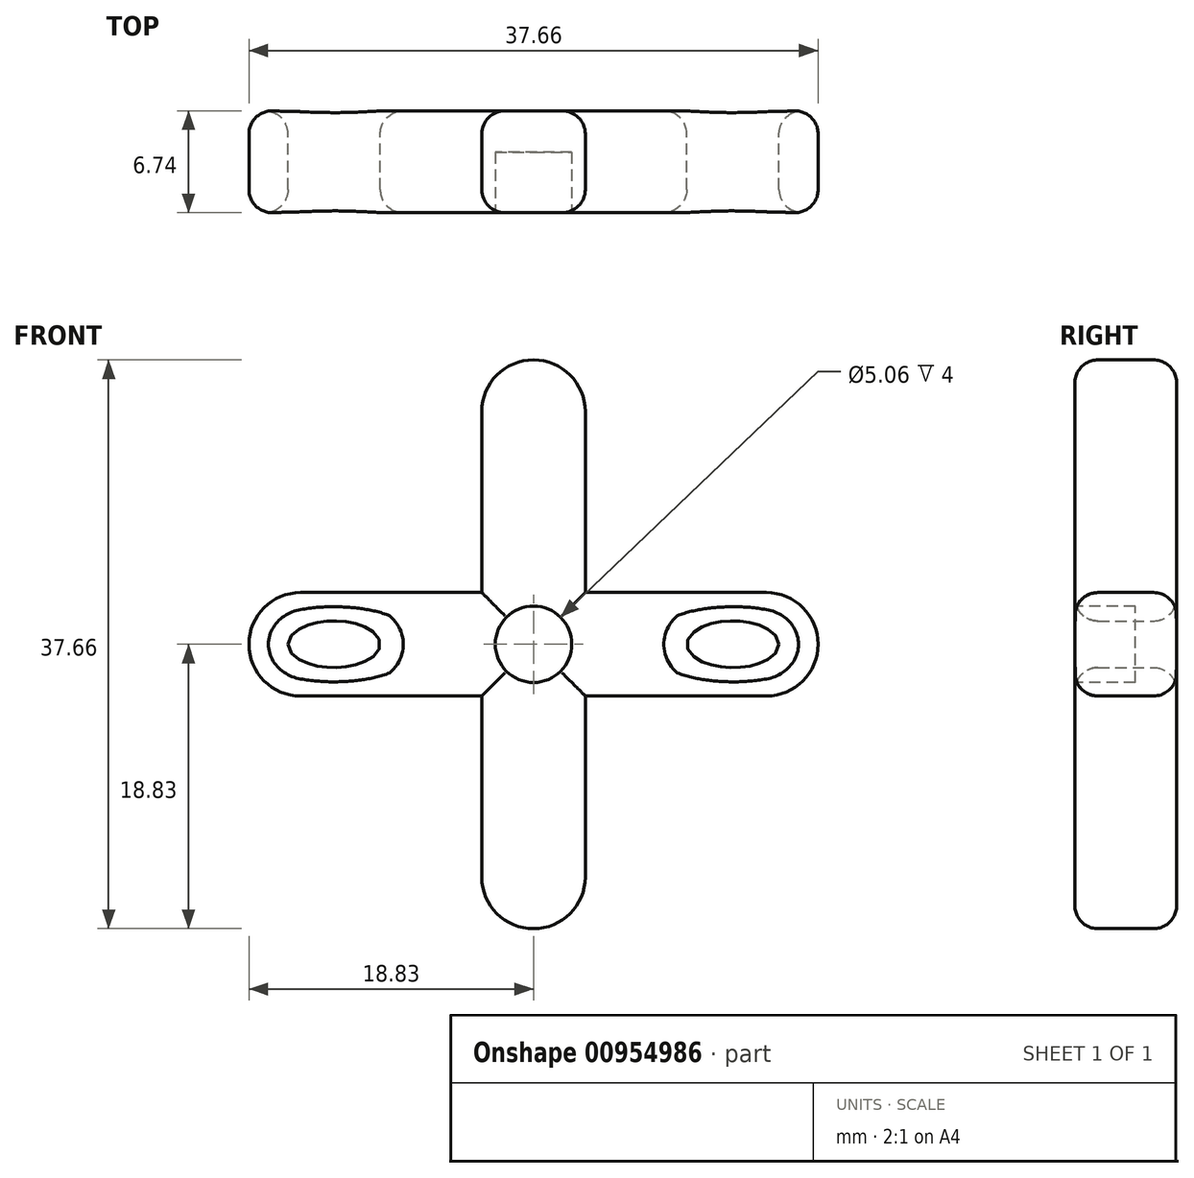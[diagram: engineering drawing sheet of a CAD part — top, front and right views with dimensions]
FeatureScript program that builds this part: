
annotation { "Feature Type Name" : "Feature", "Feature Type Description" : "" }
export const myFeature = defineFeature(function(context is Context, id is Id, definition is map)
    precondition{}
    {
        {
            var Q0;
            Q0=qCreatedBy(makeId("Front.planeOp"),FACE);
            var sketch = newSketch(context, id + "F0", { "sketchPlane" : qUnion([Q0])});
            skLineSegment(sketch, "E0.bottom", {"start": v(11.43, 2.54) * mm, "end": v(-11.43, 2.54) * mm});
            skLineSegment(sketch, "E0.top", {"start": v(11.43, -2.54) * mm, "end": v(-11.43, -2.54) * mm});
            skLineSegment(sketch, "E0.left", {"start": v(11.43, 2.54) * mm, "end": v(11.43, -2.54) * mm});
            skLineSegment(sketch, "E0.right", {"start": v(-11.43, 2.54) * mm, "end": v(-11.43, -2.54) * mm});
            skPoint(sketch, "E0.middle", {"position": v(0, 0) * mm});
            skLineSegment(sketch, "E1.bottom", {"start": v(2.54, 11.43) * mm, "end": v(-2.54, 11.43) * mm});
            skLineSegment(sketch, "E1.top", {"start": v(2.54, -11.43) * mm, "end": v(-2.54, -11.43) * mm});
            skLineSegment(sketch, "E1.left", {"start": v(2.54, 11.43) * mm, "end": v(2.54, -11.43) * mm});
            skLineSegment(sketch, "E1.right", {"start": v(-2.54, 11.43) * mm, "end": v(-2.54, -11.43) * mm});
            skArc(sketch, "E2", {"start": v(11.43, 2.54) * mm, "mid": v(13.97, 0) * mm, "end": v(11.43, -2.54) * mm});
            skArc(sketch, "E3", {"start": v(-11.43, 2.54) * mm, "mid": v(-13.97, 0) * mm, "end": v(-11.43, -2.54) * mm});
            skArc(sketch, "E4", {"start": v(2.54, 11.43) * mm, "mid": v(0, 13.97) * mm, "end": v(-2.54, 11.43) * mm});
            skArc(sketch, "E5", {"start": v(-2.54, -11.43) * mm, "mid": v(0, -13.97) * mm, "end": v(2.54, -11.43) * mm});
            skEllipse(sketch, "E6", {"center": v(9.79, 0) * mm, "majorRadius": 2.26 * mm, "minorRadius": 1.15 * mm, "majorAxis": v(1, 0)});
            skEllipse(sketch, "E7.MirrorC", {"center": v(9.79, 0) * mm, "majorRadius": 2.26 * mm, "minorRadius": 1.15 * mm, "majorAxis": v(-1, 0)});
            skEllipse(sketch, "E8.MirrorC", {"center": v(-9.79, 0) * mm, "majorRadius": 2.26 * mm, "minorRadius": 1.15 * mm, "majorAxis": v(-1, 0)});
            skEllipse(sketch, "E9", {"center": v(0, 8.8) * mm, "majorRadius": 1.78 * mm, "minorRadius": 1.1 * mm, "majorAxis": v(0, 1)});
            skEllipse(sketch, "E10.MirrorC", {"center": v(0, -8.8) * mm, "majorRadius": 1.78 * mm, "minorRadius": 1.1 * mm, "majorAxis": v(0, -1)});
            skFitSpline(sketch, "E11.0", {"points": [v(0.5, 10.6) * mm, v(0, 10.76) * mm, v(-0.5, 10.6) * mm, v(-0.9, 10.15) * mm, v(-1.16, 9.53) * mm, v(-1.25, 8.8) * mm, v(-1.16, 8.07) * mm, v(-0.9, 7.44) * mm, v(-0.5, 7) * mm, v(0, 6.83) * mm, v(0.5, 7) * mm, v(0.9, 7.44) * mm, v(1.16, 8.07) * mm, v(1.25, 8.8) * mm, v(1.16, 9.53) * mm, v(0.9, 10.15) * mm, v(0.5, 10.6) * mm, v(0, 10.76) * mm, v(-0.5, 10.6) * mm, v(0.5, 10.6) * mm]});
            skEllipse(sketch, "E12.MirrorC", {"center": v(9.79, 0) * mm, "majorRadius": 2.26 * mm, "minorRadius": 1.15 * mm, "majorAxis": v(-1, 0)});
            skFitSpline(sketch, "E13.0", {"points": [v(12.14, -0.27) * mm, v(12.2, 0) * mm, v(12.14, 0.27) * mm, v(11.94, 0.6) * mm, v(11.49, 0.95) * mm, v(10.7, 1.21) * mm, v(9.79, 1.3) * mm, v(8.88, 1.21) * mm, v(8.1, 0.95) * mm, v(7.64, 0.6) * mm, v(7.44, 0.27) * mm, v(7.38, 0) * mm, v(7.44, -0.27) * mm, v(7.64, -0.6) * mm, v(8.1, -0.95) * mm, v(8.88, -1.21) * mm, v(9.79, -1.3) * mm, v(10.7, -1.21) * mm, v(11.49, -0.95) * mm, v(11.94, -0.6) * mm, v(12.14, -0.27) * mm, v(12.2, 0) * mm, v(12.14, 0.27) * mm, v(12.14, -0.27) * mm]});
            skFitSpline(sketch, "E14.0", {"points": [v(-12.15, 0.27) * mm, v(-12.2, 0) * mm, v(-12.15, -0.27) * mm, v(-11.94, -0.6) * mm, v(-11.49, -0.95) * mm, v(-10.7, -1.21) * mm, v(-9.79, -1.3) * mm, v(-8.87, -1.21) * mm, v(-8.1, -0.95) * mm, v(-7.64, -0.6) * mm, v(-7.43, -0.27) * mm, v(-7.38, 0) * mm, v(-7.43, 0.27) * mm, v(-7.64, 0.6) * mm, v(-8.1, 0.95) * mm, v(-8.87, 1.21) * mm, v(-9.79, 1.3) * mm, v(-10.7, 1.21) * mm, v(-11.49, 0.95) * mm, v(-11.94, 0.6) * mm, v(-12.15, 0.27) * mm, v(-12.2, 0) * mm, v(-12.15, -0.27) * mm, v(-12.15, 0.27) * mm]});
            skFitSpline(sketch, "E15.0", {"points": [v(-0.52, -10.61) * mm, v(0, -10.78) * mm, v(0.52, -10.61) * mm, v(0.93, -10.16) * mm, v(1.18, -9.53) * mm, v(1.27, -8.8) * mm, v(1.18, -8.06) * mm, v(0.93, -7.43) * mm, v(0.52, -6.98) * mm, v(0, -6.8) * mm, v(-0.52, -6.98) * mm, v(-0.93, -7.43) * mm, v(-1.18, -8.06) * mm, v(-1.27, -8.8) * mm, v(-1.18, -9.53) * mm, v(-0.93, -10.16) * mm, v(-0.52, -10.61) * mm, v(0, -10.78) * mm, v(0.52, -10.61) * mm, v(-0.52, -10.61) * mm]});
            skSolve(sketch);
        }
        {
            var Q0;
            Q0=makeQuery(id+"F0.imprint","IMPRINT",FACE,{"disambiguationData":[TD([[makeQuery(id+"F0.imprint","IMPRINT",EDGE,{"derivedFrom":sQuery(id+"F0.wireOp",EDGE,"E1.bottom")}),-1.0]])]});
            var Q1;
            {var subQ0=sQuery(id+"F0.wireOp",EDGE,"E12.MirrorC");var subQ1=sQuery(id+"F0.wireOp",EDGE,"E0.left");var subQ2=makeQuery(id+"F0.imprint","INTERSECT",VERTEX,{"disambiguationData":[OD(0.0)],"derivedFrom":[subQ1,subQ0]});Q1=makeQuery(id+"F0.imprint","IMPRINT",FACE,{"disambiguationData":[TD([[makeQuery(id+"F0.imprint","IMPRINT",EDGE,{"disambiguationData":[TD([[subQ2,-1.0]])],"derivedFrom":subQ1}),-1.0]])]});}
            var Q2;
            {var subQ2=sQuery(id+"F0.wireOp",EDGE,"E1.top");Q2=makeQuery(id+"F0.imprint","IMPRINT",FACE,{"disambiguationData":[TD([[makeQuery(id+"F0.imprint","IMPRINT",EDGE,{"derivedFrom":subQ2}),-1.0]])]});}
            var Q3;
            {var subQ0=sQuery(id+"F0.wireOp",EDGE,"E3");Q3=makeQuery(id+"F0.imprint","IMPRINT",FACE,{"disambiguationData":[TD([[makeQuery(id+"F0.imprint","IMPRINT",EDGE,{"derivedFrom":subQ0}),1.0]])]});}
            var Q4;
            Q4=makeQuery(id+"F0.imprint","IMPRINT",FACE,{"disambiguationData":[TD([[makeQuery(id+"F0.imprint","IMPRINT",EDGE,{"derivedFrom":sQuery(id+"F0.wireOp",EDGE,"E9")}),1.0]])]});
            var Q5;
            {var subQ0=sQuery(id+"F0.wireOp",EDGE,"E1.left");var subQ1=sQuery(id+"F0.wireOp",EDGE,"E0.bottom");var subQ2=makeQuery(id+"F0.imprint","INTERSECT",VERTEX,{"derivedFrom":[subQ1,subQ0]});Q5=makeQuery(id+"F0.imprint","IMPRINT",FACE,{"disambiguationData":[TD([[makeQuery(id+"F0.imprint","IMPRINT",EDGE,{"disambiguationData":[TD([[subQ2,-1.0]])],"derivedFrom":subQ1}),1.0]])]});}
            var Q6;
            Q6=makeQuery(id+"F0.imprint","IMPRINT",FACE,{"disambiguationData":[TD([[makeQuery(id+"F0.imprint","IMPRINT",EDGE,{"derivedFrom":sQuery(id+"F0.wireOp",EDGE,"E1.top")}),1.0]])]});
            var Q7;
            {var subQ0=sQuery(id+"F0.wireOp",EDGE,"E2");Q7=makeQuery(id+"F0.imprint","IMPRINT",FACE,{"disambiguationData":[TD([[makeQuery(id+"F0.imprint","IMPRINT",EDGE,{"derivedFrom":subQ0}),-1.0]])]});}
            var Q8;
            {var subQ0=sQuery(id+"F0.wireOp",EDGE,"E8.MirrorC");var subQ1=sQuery(id+"F0.wireOp",EDGE,"E0.right");var subQ2=makeQuery(id+"F0.imprint","INTERSECT",VERTEX,{"disambiguationData":[OD(0.0)],"derivedFrom":[subQ1,subQ0]});Q8=makeQuery(id+"F0.imprint","IMPRINT",FACE,{"disambiguationData":[TD([[makeQuery(id+"F0.imprint","IMPRINT",EDGE,{"disambiguationData":[TD([[subQ2,-1.0]])],"derivedFrom":subQ1}),1.0]])]});}
            var Q9;
            {var subQ2=sQuery(id+"F0.wireOp",EDGE,"E0.bottom");var subQ6=sQuery(id+"F0.wireOp",EDGE,"E1.right");var subQ7=makeQuery(id+"F0.imprint","INTERSECT",VERTEX,{"derivedFrom":[subQ2,subQ6]});Q9=makeQuery(id+"F0.imprint","IMPRINT",FACE,{"disambiguationData":[TD([[makeQuery(id+"F0.imprint","IMPRINT",EDGE,{"disambiguationData":[TD([[subQ7,-1.0]])],"derivedFrom":subQ6}),-1.0]])]});}
            var Q10;
            {var subQ2=sQuery(id+"F0.wireOp",EDGE,"E0.bottom");var subQ8=sQuery(id+"F0.wireOp",EDGE,"E1.left");var subQ11=makeQuery(id+"F0.imprint","INTERSECT",VERTEX,{"derivedFrom":[subQ2,subQ8]});Q10=makeQuery(id+"F0.imprint","IMPRINT",FACE,{"disambiguationData":[TD([[makeQuery(id+"F0.imprint","IMPRINT",EDGE,{"disambiguationData":[TD([[subQ11,-1.0]])],"derivedFrom":subQ8}),1.0]])]});}
            var Q11;
            Q11=makeQuery(id+"F0.imprint","IMPRINT",FACE,{"disambiguationData":[TD([[makeQuery(id+"F0.imprint","IMPRINT",EDGE,{"derivedFrom":sQuery(id+"F0.wireOp",EDGE,"E10.MirrorC")}),1.0]])]});
            var Q12;
            {var subQ2=sQuery(id+"F0.wireOp",EDGE,"E1.bottom");Q12=makeQuery(id+"F0.imprint","IMPRINT",FACE,{"disambiguationData":[TD([[makeQuery(id+"F0.imprint","IMPRINT",EDGE,{"derivedFrom":subQ2}),1.0]])]});}
            var Q13;
            {var subQ0=sQuery(id+"F0.wireOp",EDGE,"E13.0");var subQ1=sQuery(id+"F0.wireOp",EDGE,"E0.left");var subQ2=makeQuery(id+"F0.imprint","INTERSECT",VERTEX,{"disambiguationData":[OD(0.0)],"derivedFrom":[subQ1,subQ0]});Q13=makeQuery(id+"F0.imprint","IMPRINT",FACE,{"disambiguationData":[TD([[makeQuery(id+"F0.imprint","IMPRINT",EDGE,{"disambiguationData":[TD([[subQ2,-1.0]])],"derivedFrom":subQ1}),-1.0]])]});}
            var Q14;
            {var subQ0=sQuery(id+"F0.wireOp",EDGE,"E8.MirrorC");var subQ1=sQuery(id+"F0.wireOp",EDGE,"E0.right");var subQ2=makeQuery(id+"F0.imprint","INTERSECT",VERTEX,{"disambiguationData":[OD(0.0)],"derivedFrom":[subQ1,subQ0]});Q14=makeQuery(id+"F0.imprint","IMPRINT",FACE,{"disambiguationData":[TD([[makeQuery(id+"F0.imprint","IMPRINT",EDGE,{"disambiguationData":[TD([[subQ2,-1.0]])],"derivedFrom":subQ1}),-1.0]])]});}
            var Q15;
            {var subQ0=sQuery(id+"F0.wireOp",EDGE,"E14.0");var subQ1=sQuery(id+"F0.wireOp",EDGE,"E0.right");var subQ2=makeQuery(id+"F0.imprint","INTERSECT",VERTEX,{"disambiguationData":[OD(0.0)],"derivedFrom":[subQ1,subQ0]});Q15=makeQuery(id+"F0.imprint","IMPRINT",FACE,{"disambiguationData":[TD([[makeQuery(id+"F0.imprint","IMPRINT",EDGE,{"disambiguationData":[TD([[subQ2,-1.0]])],"derivedFrom":subQ1}),1.0]])]});}
            var Q16;
            Q16=makeQuery(id+"F0.imprint","IMPRINT",FACE,{"disambiguationData":[TD([[makeQuery(id+"F0.imprint","IMPRINT",EDGE,{"derivedFrom":sQuery(id+"F0.wireOp",EDGE,"E9")}),-1.0]])]});
            var Q17;
            {var subQ0=sQuery(id+"F0.wireOp",EDGE,"E12.MirrorC");var subQ1=sQuery(id+"F0.wireOp",EDGE,"E0.left");var subQ2=makeQuery(id+"F0.imprint","INTERSECT",VERTEX,{"disambiguationData":[OD(0.0)],"derivedFrom":[subQ1,subQ0]});Q17=makeQuery(id+"F0.imprint","IMPRINT",FACE,{"disambiguationData":[TD([[makeQuery(id+"F0.imprint","IMPRINT",EDGE,{"disambiguationData":[TD([[subQ2,-1.0]])],"derivedFrom":subQ1}),1.0]])]});}
            var Q18;
            Q18=makeQuery(id+"F0.imprint","IMPRINT",FACE,{"disambiguationData":[TD([[makeQuery(id+"F0.imprint","IMPRINT",EDGE,{"derivedFrom":sQuery(id+"F0.wireOp",EDGE,"E10.MirrorC")}),-1.0]])]});
            var Q19;
            {var subQ0=sQuery(id+"F0.wireOp",EDGE,"E13.0");var subQ1=sQuery(id+"F0.wireOp",EDGE,"E0.left");var subQ2=makeQuery(id+"F0.imprint","INTERSECT",VERTEX,{"disambiguationData":[OD(0.0)],"derivedFrom":[subQ1,subQ0]});Q19=makeQuery(id+"F0.imprint","IMPRINT",FACE,{"disambiguationData":[TD([[makeQuery(id+"F0.imprint","IMPRINT",EDGE,{"disambiguationData":[TD([[subQ2,-1.0]])],"derivedFrom":subQ1}),1.0]])]});}
            var Q20;
            {var subQ0=sQuery(id+"F0.wireOp",EDGE,"E14.0");var subQ1=sQuery(id+"F0.wireOp",EDGE,"E0.right");var subQ2=makeQuery(id+"F0.imprint","INTERSECT",VERTEX,{"disambiguationData":[OD(0.0)],"derivedFrom":[subQ1,subQ0]});Q20=makeQuery(id+"F0.imprint","IMPRINT",FACE,{"disambiguationData":[TD([[makeQuery(id+"F0.imprint","IMPRINT",EDGE,{"disambiguationData":[TD([[subQ2,-1.0]])],"derivedFrom":subQ1}),-1.0]])]});}
            extrude(context, id + "F1", {"entities" : qUnion([Q0, Q1, Q2, Q3, Q4, Q5, Q6, Q7, Q8, Q9, Q10, Q11, Q12, Q13, Q14, Q15, Q16, Q17, Q18, Q19, Q20]), "depth" : 5 * mm, "offsetDistance" : 25 * mm});
        }
        {
            var Q0;
            Q0=sQuery(id+"F0.wireOp",EDGE,"E13.0");
            var Q1;
            Q1=sQuery(id+"F0.wireOp",EDGE,"E6");
            var Q2;
            {var subQ0=sQuery(id+"F0.wireOp",EDGE,"E0.top");Q2=makeQuery(id+"F1.opExtrude","CAP_EDGE",EDGE,{"disambiguationData":[OSD([subQ0]),TDD([makeQuery(id+"F0.imprint","IMPRINT",EDGE,{"disambiguationData":[TD([[makeQuery(id+"F0.imprint","INTERSECT",VERTEX,{"derivedFrom":[subQ0,sQuery(id+"F0.wireOp",EDGE,"E1.left")]}),1.0]])],"derivedFrom":subQ0})])],"isStart":true});}
            revolve(context, id + "F2", {"bodyType" : ToolBodyType.SURFACE, "surfaceOperationType" : NewSurfaceOperationType.NEW, "surfaceEntities" : qUnion([Q0, Q1]), "axis" : qUnion([Q2]), "revolveType" : RevolveType.ONE_DIRECTION, "angle" : 25 * degree});
        }
        {
            var Q0;
            Q0=makeQuery(id+"F1.opExtrude","CAP_FACE",FACE,{"disambiguationData":[OSD([sQuery(id+"F0.wireOp",EDGE,"E0.bottom"),sQuery(id+"F0.wireOp",EDGE,"E0.top"),sQuery(id+"F0.wireOp",EDGE,"E1.left"),sQuery(id+"F0.wireOp",EDGE,"E1.right"),sQuery(id+"F0.wireOp",EDGE,"E2"),sQuery(id+"F0.wireOp",EDGE,"E3"),sQuery(id+"F0.wireOp",EDGE,"E4"),sQuery(id+"F0.wireOp",EDGE,"E5")])],"isStart":true});
            var Q1;
            Q1=makeQuery(id+"F1.opExtrude","CAP_FACE",FACE,{"disambiguationData":[OSD([sQuery(id+"F0.wireOp",EDGE,"E0.bottom"),sQuery(id+"F0.wireOp",EDGE,"E0.top"),sQuery(id+"F0.wireOp",EDGE,"E1.left"),sQuery(id+"F0.wireOp",EDGE,"E1.right"),sQuery(id+"F0.wireOp",EDGE,"E2"),sQuery(id+"F0.wireOp",EDGE,"E3"),sQuery(id+"F0.wireOp",EDGE,"E4"),sQuery(id+"F0.wireOp",EDGE,"E5")])],"isStart":false});
            fillet(context, id + "F3", {"entities" : qUnion([Q0, Q1]), "radius" : 1.13 * mm, "allowEdgeOverflow" : false});
        }
        {
            var Q0;
            Q0=sQuery(id+"F0.wireOp",EDGE,"E9");
            var Q1;
            Q1=sQuery(id+"F0.wireOp",EDGE,"E11.0");
            var Q2;
            {var subQ0=sQuery(id+"F0.wireOp",EDGE,"E4");var subQ1=sQuery(id+"F0.wireOp",EDGE,"E1.left");var subQ2=sQuery(id+"F0.wireOp",EDGE,"E0.bottom");Q2=makeQuery(id+"F3.opFillet","BLEND_EDGE",EDGE,{"blendedFrom":[makeQuery(id+"F1.opExtrude","CAP_EDGE",EDGE,{"disambiguationData":[OSD([subQ1]),TDD([makeQuery(id+"F0.imprint","IMPRINT",EDGE,{"disambiguationData":[TD([[makeQuery(id+"F0.imprint","INTERSECT",VERTEX,{"derivedFrom":[subQ2,subQ1]}),1.0]])],"derivedFrom":subQ1})])],"isStart":true}),makeQuery(id+"F1.opExtrude","CAP_FACE",FACE,{"disambiguationData":[OSD([subQ2,sQuery(id+"F0.wireOp",EDGE,"E0.top"),subQ1,sQuery(id+"F0.wireOp",EDGE,"E1.right"),sQuery(id+"F0.wireOp",EDGE,"E2"),sQuery(id+"F0.wireOp",EDGE,"E3"),subQ0,sQuery(id+"F0.wireOp",EDGE,"E5")])],"isStart":true})],"blendedInto":[makeQuery(id+"F1.opExtrude","CAP_FACE",FACE,{"disambiguationData":[OSD([subQ2,sQuery(id+"F0.wireOp",EDGE,"E0.top"),subQ1,sQuery(id+"F0.wireOp",EDGE,"E1.right"),sQuery(id+"F0.wireOp",EDGE,"E2"),sQuery(id+"F0.wireOp",EDGE,"E3"),subQ0,sQuery(id+"F0.wireOp",EDGE,"E5")])],"isStart":true})]});}
            revolve(context, id + "F4", {"bodyType" : ToolBodyType.SURFACE, "surfaceOperationType" : NewSurfaceOperationType.NEW, "surfaceEntities" : qUnion([Q0, Q1]), "axis" : qUnion([Q2]), "revolveType" : RevolveType.ONE_DIRECTION, "angle" : 25 * degree});
        }
        {
            var Q0;
            Q0=sQuery(id+"F0.wireOp",EDGE,"E8.MirrorC");
            var Q1;
            Q1=sQuery(id+"F0.wireOp",EDGE,"E14.0");
            var Q2;
            {var subQ0=sQuery(id+"F0.wireOp",EDGE,"E3");var subQ1=sQuery(id+"F0.wireOp",EDGE,"E1.right");var subQ2=sQuery(id+"F0.wireOp",EDGE,"E0.bottom");Q2=makeQuery(id+"F3.opFillet","BLEND_EDGE",EDGE,{"blendedFrom":[makeQuery(id+"F1.opExtrude","CAP_EDGE",EDGE,{"disambiguationData":[OSD([subQ2]),TDD([makeQuery(id+"F0.imprint","IMPRINT",EDGE,{"disambiguationData":[TD([[makeQuery(id+"F0.imprint","INTERSECT",VERTEX,{"derivedFrom":[subQ2,subQ1]}),-1.0]])],"derivedFrom":subQ2})])],"isStart":true}),makeQuery(id+"F1.opExtrude","CAP_FACE",FACE,{"disambiguationData":[OSD([subQ2,sQuery(id+"F0.wireOp",EDGE,"E0.top"),sQuery(id+"F0.wireOp",EDGE,"E1.left"),subQ1,sQuery(id+"F0.wireOp",EDGE,"E2"),subQ0,sQuery(id+"F0.wireOp",EDGE,"E4"),sQuery(id+"F0.wireOp",EDGE,"E5")])],"isStart":true})],"blendedInto":[makeQuery(id+"F1.opExtrude","CAP_FACE",FACE,{"disambiguationData":[OSD([subQ2,sQuery(id+"F0.wireOp",EDGE,"E0.top"),sQuery(id+"F0.wireOp",EDGE,"E1.left"),subQ1,sQuery(id+"F0.wireOp",EDGE,"E2"),subQ0,sQuery(id+"F0.wireOp",EDGE,"E4"),sQuery(id+"F0.wireOp",EDGE,"E5")])],"isStart":true})]});}
            revolve(context, id + "F5", {"bodyType" : ToolBodyType.SURFACE, "surfaceOperationType" : NewSurfaceOperationType.NEW, "surfaceEntities" : qUnion([Q0, Q1]), "axis" : qUnion([Q2]), "revolveType" : RevolveType.ONE_DIRECTION, "oppositeDirection" : true, "angle" : 25 * degree});
        }
        {
            var Q0;
            Q0=sQuery(id+"F0.wireOp",EDGE,"E10.MirrorC");
            var Q1;
            Q1=sQuery(id+"F0.wireOp",EDGE,"E15.0");
            var Q2;
            {var subQ0=sQuery(id+"F0.wireOp",EDGE,"E5");var subQ1=sQuery(id+"F0.wireOp",EDGE,"E1.right");var subQ2=sQuery(id+"F0.wireOp",EDGE,"E0.top");Q2=makeQuery(id+"F3.opFillet","BLEND_EDGE",EDGE,{"blendedFrom":[makeQuery(id+"F1.opExtrude","CAP_EDGE",EDGE,{"disambiguationData":[OSD([subQ1]),TDD([makeQuery(id+"F0.imprint","IMPRINT",EDGE,{"disambiguationData":[TD([[makeQuery(id+"F0.imprint","INTERSECT",VERTEX,{"derivedFrom":[subQ2,subQ1]}),-1.0]])],"derivedFrom":subQ1})])],"isStart":true}),makeQuery(id+"F1.opExtrude","CAP_FACE",FACE,{"disambiguationData":[OSD([sQuery(id+"F0.wireOp",EDGE,"E0.bottom"),subQ2,sQuery(id+"F0.wireOp",EDGE,"E1.left"),subQ1,sQuery(id+"F0.wireOp",EDGE,"E2"),sQuery(id+"F0.wireOp",EDGE,"E3"),sQuery(id+"F0.wireOp",EDGE,"E4"),subQ0])],"isStart":true})],"blendedInto":[makeQuery(id+"F1.opExtrude","CAP_FACE",FACE,{"disambiguationData":[OSD([sQuery(id+"F0.wireOp",EDGE,"E0.bottom"),subQ2,sQuery(id+"F0.wireOp",EDGE,"E1.left"),subQ1,sQuery(id+"F0.wireOp",EDGE,"E2"),sQuery(id+"F0.wireOp",EDGE,"E3"),sQuery(id+"F0.wireOp",EDGE,"E4"),subQ0])],"isStart":true})]});}
            revolve(context, id + "F6", {"bodyType" : ToolBodyType.SURFACE, "surfaceOperationType" : NewSurfaceOperationType.NEW, "surfaceEntities" : qUnion([Q0, Q1]), "axis" : qUnion([Q2]), "revolveType" : RevolveType.ONE_DIRECTION, "oppositeDirection" : true, "angle" : 25 * degree});
        }
        {
            var Q0;
            Q0=makeQuery(id+"F4.opRevolve","SWEPT_BODY",BODY,{"disambiguationData":[OSD([sQuery(id+"F0.wireOp",EDGE,"E9")])]});
            var Q1;
            Q1=makeQuery(id+"F2.opRevolve","SWEPT_BODY",BODY,{"disambiguationData":[OSD([sQuery(id+"F0.wireOp",EDGE,"E13.0")])]});
            var Q2;
            Q2=makeQuery(id+"F1.opExtrude","SWEPT_BODY",BODY,{"disambiguationData":[OSD([sQuery(id+"F0.wireOp",EDGE,"E0.bottom"),sQuery(id+"F0.wireOp",EDGE,"E0.top"),sQuery(id+"F0.wireOp",EDGE,"E1.left"),sQuery(id+"F0.wireOp",EDGE,"E1.right"),sQuery(id+"F0.wireOp",EDGE,"E2"),sQuery(id+"F0.wireOp",EDGE,"E3"),sQuery(id+"F0.wireOp",EDGE,"E4"),sQuery(id+"F0.wireOp",EDGE,"E5")])]});
            var Q3;
            Q3=makeQuery(id+"F4.opRevolve","SWEPT_BODY",BODY,{"disambiguationData":[OSD([sQuery(id+"F0.wireOp",EDGE,"E11.0")])]});
            var Q4;
            Q4=makeQuery(id+"F5.opRevolve","SWEPT_BODY",BODY,{"disambiguationData":[OSD([sQuery(id+"F0.wireOp",EDGE,"E8.MirrorC")])]});
            var Q5;
            Q5=makeQuery(id+"F5.opRevolve","SWEPT_BODY",BODY,{"disambiguationData":[OSD([sQuery(id+"F0.wireOp",EDGE,"E14.0")])]});
            var Q6;
            Q6=makeQuery(id+"F2.opRevolve","SWEPT_BODY",BODY,{"disambiguationData":[OSD([sQuery(id+"F0.wireOp",EDGE,"E6")])]});
            var Q7;
            Q7=makeQuery(id+"F6.opRevolve","SWEPT_BODY",BODY,{"disambiguationData":[OSD([sQuery(id+"F0.wireOp",EDGE,"E10.MirrorC")])]});
            var Q8;
            Q8=makeQuery(id+"F6.opRevolve","SWEPT_BODY",BODY,{"disambiguationData":[OSD([sQuery(id+"F0.wireOp",EDGE,"E15.0")])]});
            var Q9;
            Q9=qCreatedBy(makeId("Origin.pointOp"),VERTEX);
            transform(context, id + "F7", {"entities" : qUnion([Q0, Q1, Q2, Q3, Q4, Q5, Q6, Q7, Q8]), "transformType" : TransformType.SCALE_UNIFORMLY, "scale" : 1.35, "scalePoint" : qUnion([Q9]), "makeCopy" : false});
        }
        {
            var Q0;
            Q0=makeQuery(id+"F1.opExtrude","CAP_FACE",FACE,{"disambiguationData":[OSD([sQuery(id+"F0.wireOp",EDGE,"E0.bottom"),sQuery(id+"F0.wireOp",EDGE,"E0.top"),sQuery(id+"F0.wireOp",EDGE,"E1.left"),sQuery(id+"F0.wireOp",EDGE,"E1.right"),sQuery(id+"F0.wireOp",EDGE,"E2"),sQuery(id+"F0.wireOp",EDGE,"E3"),sQuery(id+"F0.wireOp",EDGE,"E4"),sQuery(id+"F0.wireOp",EDGE,"E5")])],"isStart":false});
            var sketch = newSketch(context, id + "F8", { "sketchPlane" : qUnion([Q0])});
            skCircle(sketch, "E16", {"center": v(0, 0) * mm, "radius": 2.78 * mm});
            skCircle(sketch, "E17", {"center": v(0, 0) * mm, "radius": 2.53 * mm});
            skSolve(sketch);
        }
        {
            var Q0;
            Q0=makeQuery(id+"F8.imprint","IMPRINT",FACE,{"disambiguationData":[TD([[makeQuery(id+"F8.imprint","IMPRINT",EDGE,{"derivedFrom":sQuery(id+"F8.wireOp",EDGE,"E17")}),1.0]])]});
            extrude(context, id + "F9", {"entities" : qUnion([Q0]), "operationType" : NewBodyOperationType.REMOVE, "oppositeDirection" : true, "depth" : 4 * mm, "offsetDistance" : 25 * mm});
        }
    });
